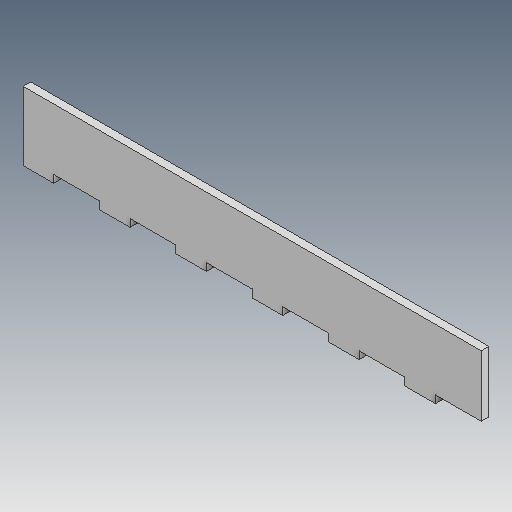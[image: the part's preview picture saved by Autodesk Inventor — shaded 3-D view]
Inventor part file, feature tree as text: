
AUTODESK INVENTOR PART (.ipt)
format: ipt  version: 2020 (Build 240168000, 168)  size: 130,560 bytes
history: native  units: mm
features: extrude x2, sketch x2
ambient origin geometry x8: Origin, YZ Plane, XZ Plane, XY Plane, X Axis, Y Axis, Z Axis, Center Point
bodies: Solid1 (feature_tree)
feature tree (4):
  extrude  "Base"  Depth=40.0mm
  extrude  "Encaixe"  Depth=20.0mm
  sketch  "Sketch1"  dims[d0=300.0mm d1=40.0mm]
  sketch  "Sketch2"  dims[d2=5.0mm d3=0.0mm d4=20.0mm d5=5.0mm d6=60.0mm d8=50.0mm d9=10.0mm d11=10.0mm d13=5.0mm d14=0.0mm]
